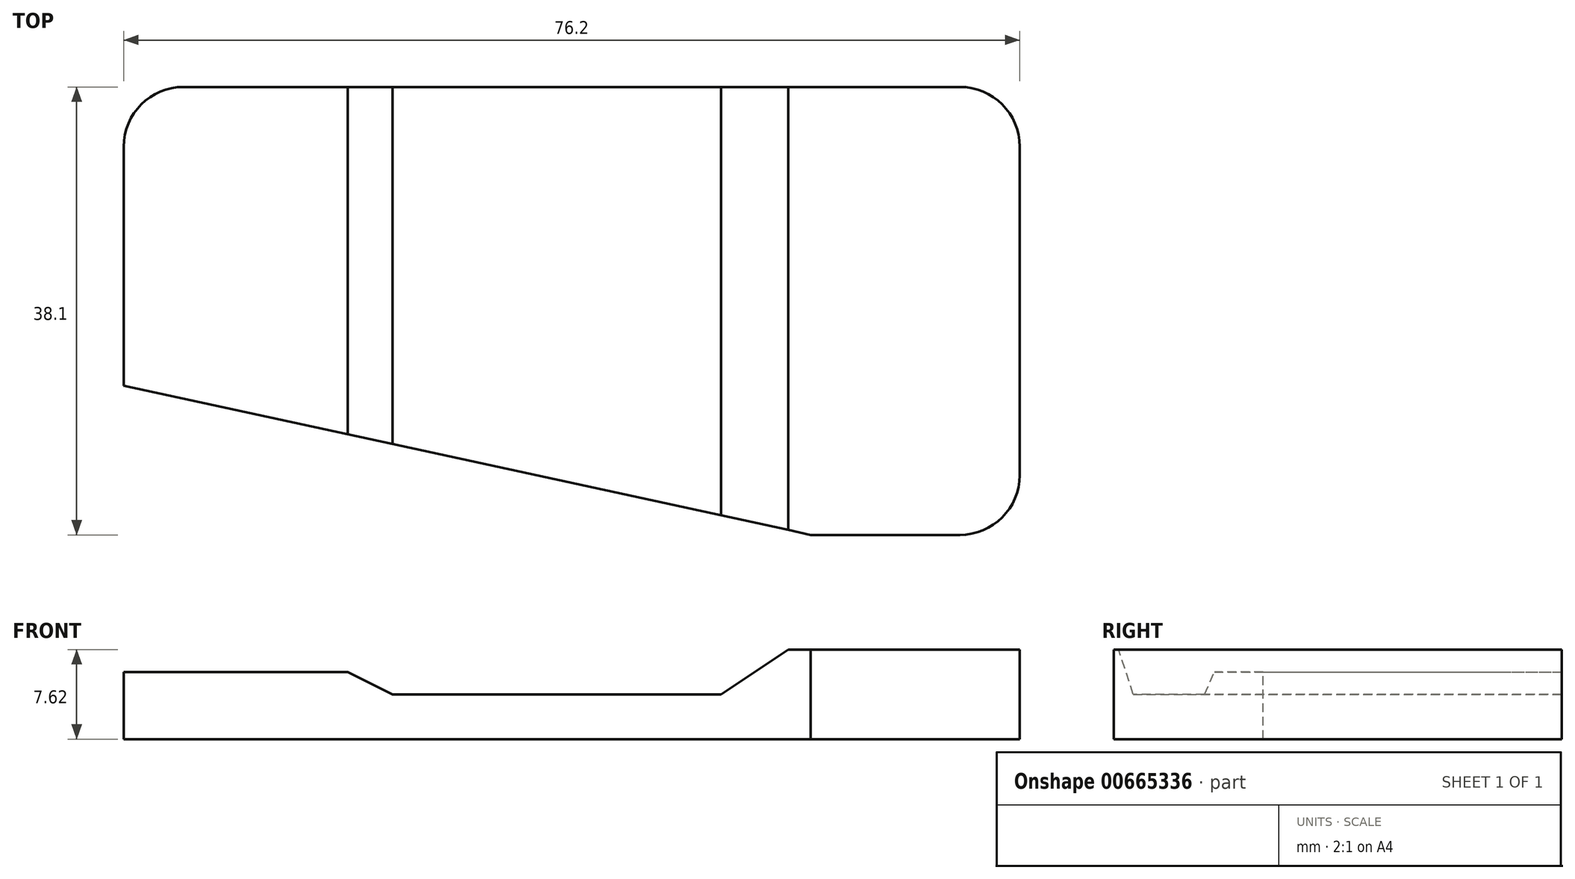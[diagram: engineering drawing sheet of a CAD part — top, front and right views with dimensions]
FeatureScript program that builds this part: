
annotation { "Feature Type Name" : "Feature", "Feature Type Description" : "" }
export const myFeature = defineFeature(function(context is Context, id is Id, definition is map)
    precondition{}
    {
        {
            var Q0;
            Q0=qCreatedBy(makeId("Top.planeOp"),FACE);
            var sketch = newSketch(context, id + "F0", { "sketchPlane" : qUnion([Q0])});
            skLineSegment(sketch, "E0.bottom", {"start": v(38.1, -19.05) * mm, "end": v(-38.1, -19.05) * mm});
            skLineSegment(sketch, "E0.top", {"start": v(38.1, 19.05) * mm, "end": v(-38.1, 19.05) * mm});
            skLineSegment(sketch, "E0.left", {"start": v(38.1, -19.05) * mm, "end": v(38.1, 19.05) * mm});
            skLineSegment(sketch, "E0.right", {"start": v(-38.1, -19.05) * mm, "end": v(-38.1, 19.05) * mm});
            skPoint(sketch, "E0.middle", {"position": v(0, 0) * mm});
            skSolve(sketch);
        }
        {
            var Q0;
            Q0=makeQuery(id+"F0.imprint","IMPRINT",FACE,{"disambiguationData":[TD([[makeQuery(id+"F0.imprint","IMPRINT",EDGE,{"derivedFrom":sQuery(id+"F0.wireOp",EDGE,"E0.bottom")}),-1.0]])]});
            extrude(context, id + "F1", {"entities" : qUnion([Q0]), "depth" : 7.62 * mm, "offsetDistance" : 25.4 * mm});
        }
        {
            var Q0;
            Q0=makeQuery(id+"F1.opExtrude","CAP_FACE",FACE,{"disambiguationData":[OSD([sQuery(id+"F0.wireOp",EDGE,"E0.bottom"),sQuery(id+"F0.wireOp",EDGE,"E0.top"),sQuery(id+"F0.wireOp",EDGE,"E0.left"),sQuery(id+"F0.wireOp",EDGE,"E0.right")])],"isStart":false});
            var sketch = newSketch(context, id + "F2", { "sketchPlane" : qUnion([Q0])});
            skLineSegment(sketch, "E1.bottom", {"start": v(20.32, -19.05) * mm, "end": v(-20.32, -19.05) * mm});
            skLineSegment(sketch, "E1.top", {"start": v(20.32, 19.05) * mm, "end": v(-20.32, 19.05) * mm});
            skLineSegment(sketch, "E1.left", {"start": v(20.32, -19.05) * mm, "end": v(20.32, 19.05) * mm});
            skLineSegment(sketch, "E1.right", {"start": v(-20.32, -19.05) * mm, "end": v(-20.32, 19.05) * mm});
            skPoint(sketch, "E1.middle", {"position": v(0, 0) * mm});
            skLineSegment(sketch, "E2.left", {"start": v(-20.32, 19.05) * mm, "end": v(-20.32, -19.05) * mm});
            skSolve(sketch);
        }
        {
            var Q0;
            {var subQ0=sQuery(id+"F2.wireOp",EDGE,"E1.left");Q0=makeQuery(id+"F2.imprint","IMPRINT",FACE,{"disambiguationData":[TD([[makeQuery(id+"F2.imprint","IMPRINT",EDGE,{"derivedFrom":subQ0}),-1.0]])]});}
            var sketch = newSketch(context, id + "F3", { "sketchPlane" : qUnion([Q0])});
            skLineSegment(sketch, "E3.0", {"start": v(-38.1, -19.05) * mm, "end": v(-38.1, 19.05) * mm});
            skLineSegment(sketch, "E4.0", {"start": v(20.32, -19.05) * mm, "end": v(-20.32, -19.05) * mm});
            skLineSegment(sketch, "E5.0", {"start": v(20.32, -19.05) * mm, "end": v(-38.1, -19.05) * mm});
            skPoint(sketch, "E6.orphan", {"position": v(38.1, -19.05) * mm});
            skLineSegment(sketch, "E7", {"start": v(-38.1, -6.35) * mm, "end": v(20.32, -19.05) * mm});
            skSolve(sketch);
        }
        {
            var Q0;
            {var subQ3=sQuery(id+"F3.wireOp",EDGE,"cd232530-1e49-4a57-8ab3-45a062eee770");Q0=makeQuery(id+"F3.imprint","IMPRINT",FACE,{"disambiguationData":[TD([[makeQuery(id+"F3.imprint","IMPRINT",EDGE,{"derivedFrom":subQ3}),-1.0]])]});}
            var Q1;
            {var subQ3=sQuery(id+"F3.wireOp",EDGE,"E7");Q1=makeQuery(id+"F3.imprint","IMPRINT",FACE,{"disambiguationData":[TD([[makeQuery(id+"F3.imprint","IMPRINT",EDGE,{"derivedFrom":subQ3}),-1.0]])]});}
            extrude(context, id + "F4", {"entities" : qUnion([Q0, Q1]), "operationType" : NewBodyOperationType.REMOVE, "endBound" : BoundingType.THROUGH_ALL, "oppositeDirection" : true, "depth" : 25.4 * mm, "offsetDistance" : 25.4 * mm});
        }
        {
            var Q0;
            Q0=makeQuery(id+"F1.opExtrude","SWEPT_FACE",FACE,{"disambiguationData":[OSD([sQuery(id+"F0.wireOp",EDGE,"E0.top")])]});
            var sketch = newSketch(context, id + "F5", { "sketchPlane" : qUnion([Q0])});
            skPoint(sketch, "E8.0", {"position": v(-20.32, 7.62) * mm});
            skPoint(sketch, "E9.0", {"position": v(20.32, 7.62) * mm});
            skLineSegment(sketch, "E10", {"start": v(-20.32, 7.62) * mm, "end": v(-20.32, 3.81) * mm});
            skLineSegment(sketch, "E11", {"start": v(20.32, 5.72) * mm, "end": v(20.32, 3.81) * mm});
            skLineSegment(sketch, "E12", {"start": v(-20.32, 3.81) * mm, "end": v(20.32, 3.81) * mm});
            skLineSegment(sketch, "E13", {"start": v(20.32, 5.72) * mm, "end": v(38.1, 5.72) * mm});
            skSolve(sketch);
        }
        {
            var Q0;
            {var subQ1=sQuery(id+"F5.wireOp",EDGE,"E10");Q0=makeQuery(id+"F5.imprint","IMPRINT",FACE,{"disambiguationData":[TD([[makeQuery(id+"F5.imprint","IMPRINT",EDGE,{"derivedFrom":subQ1}),1.0]])]});}
            extrude(context, id + "F6", {"entities" : qUnion([Q0]), "operationType" : NewBodyOperationType.REMOVE, "endBound" : BoundingType.THROUGH_ALL, "oppositeDirection" : true, "depth" : 25.4 * mm, "offsetDistance" : 25.4 * mm});
        }
        {
            var Q0;
            Q0=makeQuery(id+"F6.boolean.opBoolean","COPY",EDGE,{"derivedFrom":makeQuery(id+"F6.opExtrude","SWEPT_EDGE",EDGE,{"disambiguationData":[OSD([sQuery(id+"F5.wireOp",EDGE,"E10"),sQuery(id+"F5.wireOp",EDGE,"E12")])]})});
            chamfer(context, id + "F7", {"entities" : qUnion([Q0]), "chamferType" : ChamferType.TWO_OFFSETS, "width1" : 7.62 * mm, "oppositeDirection" : false, "width2" : 5.08 * mm, "tangentPropagation" : true});
        }
        {
            var Q0;
            Q0=makeQuery(id+"F6.boolean.opBoolean","COPY",EDGE,{"derivedFrom":makeQuery(id+"F6.opExtrude","SWEPT_EDGE",EDGE,{"disambiguationData":[OSD([sQuery(id+"F5.wireOp",EDGE,"E11"),sQuery(id+"F5.wireOp",EDGE,"E12")])]})});
            chamfer(context, id + "F8", {"entities" : qUnion([Q0]), "chamferType" : ChamferType.TWO_OFFSETS, "width1" : 2.54 * mm, "oppositeDirection" : false, "width2" : 5.08 * mm, "tangentPropagation" : true});
        }
        {
            var Q0;
            Q0=makeQuery(id+"F4.boolean.opBoolean","COPY",EDGE,{"derivedFrom":makeQuery(id+"F4.opExtrude","SWEPT_EDGE",EDGE,{"disambiguationData":[OSD([sQuery(id+"F3.wireOp",EDGE,"E3.0"),sQuery(id+"F3.wireOp",EDGE,"E7")])]})});
            var Q1;
            Q1=makeQuery(id+"F1.opExtrude","SWEPT_EDGE",EDGE,{"disambiguationData":[OSD([sQuery(id+"F0.wireOp",EDGE,"E0.top"),sQuery(id+"F0.wireOp",EDGE,"E0.right")])]});
            var Q2;
            Q2=makeQuery(id+"F1.opExtrude","SWEPT_EDGE",EDGE,{"disambiguationData":[OSD([sQuery(id+"F0.wireOp",EDGE,"E0.bottom"),sQuery(id+"F0.wireOp",EDGE,"E0.left")])]});
            var Q3;
            Q3=makeQuery(id+"F1.opExtrude","SWEPT_EDGE",EDGE,{"disambiguationData":[OSD([sQuery(id+"F0.wireOp",EDGE,"E0.top"),sQuery(id+"F0.wireOp",EDGE,"E0.left")])]});
            fillet(context, id + "F9", {"entities" : qUnion([Q0, Q1, Q2, Q3]), "radius" : 5.08 * mm, "tangentPropagation" : true, "allowEdgeOverflow" : false});
        }
    });
